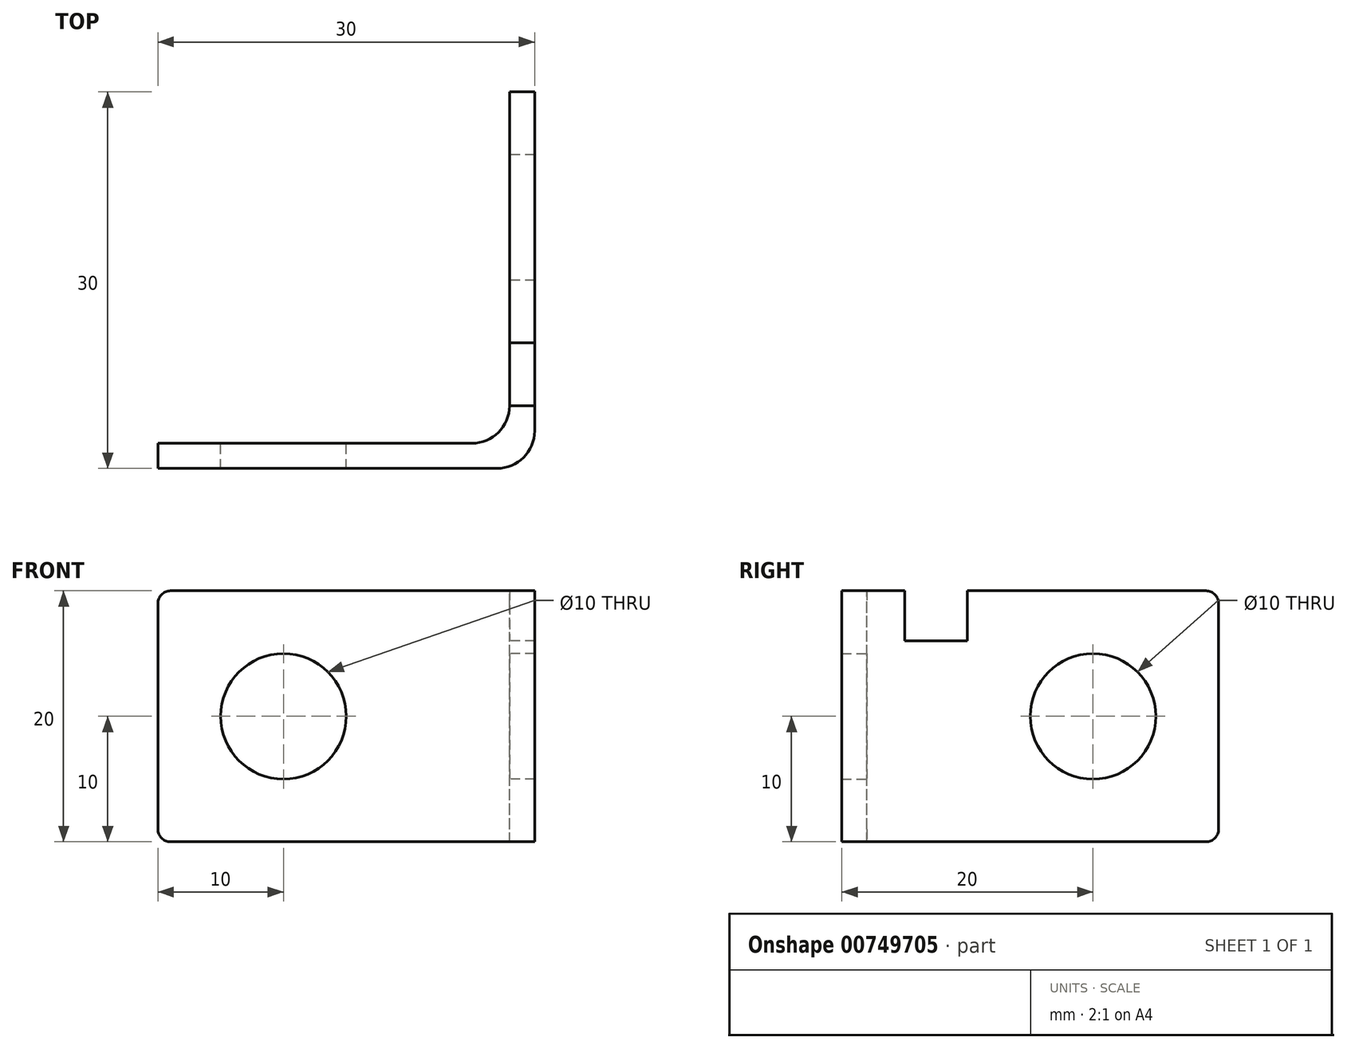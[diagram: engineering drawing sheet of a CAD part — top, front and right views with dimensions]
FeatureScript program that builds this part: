
annotation { "Feature Type Name" : "Feature", "Feature Type Description" : "" }
export const myFeature = defineFeature(function(context is Context, id is Id, definition is map)
    precondition{}
    {
        {
            var Q0;
            Q0=qCreatedBy(makeId("Right.planeOp"),FACE);
            var sketch = newSketch(context, id + "F0", { "sketchPlane" : qUnion([Q0])});
            skLineSegment(sketch, "E0.bottom", {"start": v(0, 0) * mm, "end": v(2, 0) * mm});
            skLineSegment(sketch, "E0.top", {"start": v(0, 20) * mm, "end": v(2, 20) * mm});
            skLineSegment(sketch, "E0.left", {"start": v(0, 0) * mm, "end": v(0, 20) * mm});
            skLineSegment(sketch, "E0.right", {"start": v(2, 0) * mm, "end": v(2, 20) * mm});
            skSolve(sketch);
        }
        {
            var Q0;
            Q0 = qSketchRegion(id + "F0", true);
            extrude(context, id + "F1", {"entities" : qUnion([Q0]), "depth" : 30 * mm, "offsetDistance" : 25 * mm});
        }
        {
            var Q0;
            Q0=makeQuery(id+"F1.opExtrude","CAP_FACE",FACE,{"disambiguationData":[OSD([sQuery(id+"F0.wireOp",EDGE,"E0.bottom"),sQuery(id+"F0.wireOp",EDGE,"E0.top"),sQuery(id+"F0.wireOp",EDGE,"E0.left"),sQuery(id+"F0.wireOp",EDGE,"E0.right")])],"isStart":false});
            var sketch = newSketch(context, id + "F2", { "sketchPlane" : qUnion([Q0])});
            skLineSegment(sketch, "E1.0", {"start": v(0, 20) * mm, "end": v(2, 20) * mm});
            skLineSegment(sketch, "E2.bottom", {"start": v(0, 0) * mm, "end": v(30, 0) * mm});
            skLineSegment(sketch, "E2.top", {"start": v(0, 20) * mm, "end": v(30, 20) * mm});
            skLineSegment(sketch, "E2.left", {"start": v(0, 0) * mm, "end": v(0, 20) * mm});
            skLineSegment(sketch, "E2.right", {"start": v(30, 0) * mm, "end": v(30, 20) * mm});
            skSolve(sketch);
        }
        {
            var Q0;
            Q0 = qSketchRegion(id + "F2", true);
            extrude(context, id + "F3", {"entities" : qUnion([Q0]), "operationType" : NewBodyOperationType.ADD, "oppositeDirection" : true, "depth" : 2 * mm, "offsetDistance" : 25 * mm});
        }
        {
            var Q0;
            Q0=makeQuery(id+"F1.opExtrude","SWEPT_FACE",FACE,{"disambiguationData":[OSD([sQuery(id+"F0.wireOp",EDGE,"E0.right")])]});
            var sketch = newSketch(context, id + "F4", { "sketchPlane" : qUnion([Q0])});
            skCircle(sketch, "E3", {"center": v(-10, 10) * mm, "radius": 5 * mm});
            skSolve(sketch);
        }
        {
            var Q0;
            Q0 = qSketchRegion(id + "F4", true);
            extrude(context, id + "F5", {"entities" : qUnion([Q0]), "operationType" : NewBodyOperationType.REMOVE, "endBound" : BoundingType.THROUGH_ALL, "oppositeDirection" : true, "depth" : 25 * mm, "offsetDistance" : 25 * mm});
        }
        {
            var Q0;
            Q0=makeQuery(id+"F3.opExtrude","CAP_FACE",FACE,{"disambiguationData":[OSD([sQuery(id+"F2.wireOp",EDGE,"E2.bottom"),sQuery(id+"F2.wireOp",EDGE,"E2.top"),sQuery(id+"F2.wireOp",EDGE,"E2.left"),sQuery(id+"F2.wireOp",EDGE,"E2.right")])],"isStart":false});
            var sketch = newSketch(context, id + "F6", { "sketchPlane" : qUnion([Q0])});
            skCircle(sketch, "E4", {"center": v(-20, 10) * mm, "radius": 5 * mm});
            skLineSegment(sketch, "E5.bottom", {"start": v(-5, 20) * mm, "end": v(-10, 20) * mm});
            skLineSegment(sketch, "E5.top", {"start": v(-5, 16) * mm, "end": v(-10, 16) * mm});
            skLineSegment(sketch, "E5.left", {"start": v(-5, 20) * mm, "end": v(-5, 16) * mm});
            skLineSegment(sketch, "E5.right", {"start": v(-10, 20) * mm, "end": v(-10, 16) * mm});
            skSolve(sketch);
        }
        {
            var Q0;
            Q0 = qSketchRegion(id + "F6", true);
            extrude(context, id + "F7", {"entities" : qUnion([Q0]), "operationType" : NewBodyOperationType.REMOVE, "endBound" : BoundingType.THROUGH_ALL, "oppositeDirection" : true, "depth" : 25 * mm, "offsetDistance" : 25 * mm});
        }
        {
            var Q0;
            Q0=makeQuery(id+"F1.opExtrude","CAP_EDGE",EDGE,{"disambiguationData":[OSD([sQuery(id+"F0.wireOp",EDGE,"E0.top")])],"isStart":true});
            var Q1;
            Q1=makeQuery(id+"F3.opExtrude","SWEPT_EDGE",EDGE,{"disambiguationData":[OSD([sQuery(id+"F2.wireOp",EDGE,"E2.top"),sQuery(id+"F2.wireOp",EDGE,"E2.right")])]});
            var Q2;
            Q2=makeQuery(id+"F3.opExtrude","SWEPT_EDGE",EDGE,{"disambiguationData":[OSD([sQuery(id+"F2.wireOp",EDGE,"E2.bottom"),sQuery(id+"F2.wireOp",EDGE,"E2.right")])]});
            var Q3;
            Q3=makeQuery(id+"F1.opExtrude","CAP_EDGE",EDGE,{"disambiguationData":[OSD([sQuery(id+"F0.wireOp",EDGE,"E0.bottom")])],"isStart":true});
            fillet(context, id + "F8", {"entities" : qUnion([Q0, Q1, Q2, Q3]), "radius" : 1 * mm, "tangentPropagation" : true, "allowEdgeOverflow" : false});
        }
        {
            var Q0;
            Q0=makeQuery(id+"F3.boolean.opBoolean","INTERSECT",EDGE,{"derivedFrom":[makeQuery(id+"F1.opExtrude","SWEPT_FACE",FACE,{"disambiguationData":[OSD([sQuery(id+"F0.wireOp",EDGE,"E0.right")])]}),makeQuery(id+"F3.opExtrude","CAP_FACE",FACE,{"disambiguationData":[OSD([sQuery(id+"F2.wireOp",EDGE,"E2.bottom"),sQuery(id+"F2.wireOp",EDGE,"E2.top"),sQuery(id+"F2.wireOp",EDGE,"E2.left"),sQuery(id+"F2.wireOp",EDGE,"E2.right")])],"isStart":false})]});
            var Q1;
            Q1=makeQuery(id+"F1.opExtrude","CAP_EDGE",EDGE,{"disambiguationData":[OSD([sQuery(id+"F0.wireOp",EDGE,"E0.left")])],"isStart":false});
            fillet(context, id + "F9", {"entities" : qUnion([Q0, Q1]), "radius" : 3 * mm, "tangentPropagation" : true, "allowEdgeOverflow" : false});
        }
    });
